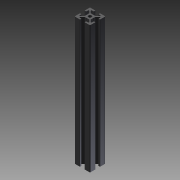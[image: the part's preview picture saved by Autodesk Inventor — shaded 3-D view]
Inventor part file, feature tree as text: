
AUTODESK INVENTOR PART (.ipt)
format: ipt  version: 2014 SP1 (Build 180222100, 222)  size: 172,032 bytes
history: native  units: mm
features: other x7, sketch x2, extrude x1, revolve x1
ambient origin geometry x8: Origin, YZ Plane, XZ Plane, XY Plane, X Axis, Y Axis, Z Axis, Center Point
bodies: Solid1 (feature_tree)
feature tree (11):
  extrude  "Extrusion1"  TaperAngle=360.0deg  [1 undecoded]
  revolve  "Revolution1"  [1 undecoded]
  other  "C1_XY"
  other  "C1_YZ"
  other  "C1_ZX"
  other  "C1_X"
  other  "C1_Y"
  other  "C1_Z"
  other  "C1_Center"
  sketch  "Sketch_1"  dims[d0=165.0mm d1=0.0mm d2=360.0deg]
  sketch  "Sketch_2"
note: 2 required parameter values undecoded (feature->parameter linkage not recoverable at this tier; creation-order binding heuristic only, values carry confidence <= 0.55)
